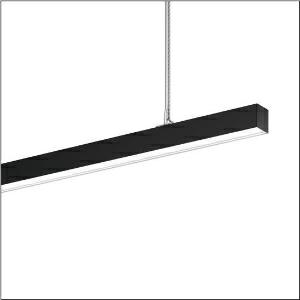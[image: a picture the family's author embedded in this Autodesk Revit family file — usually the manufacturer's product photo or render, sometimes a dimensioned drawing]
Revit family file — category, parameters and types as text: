
# Revit family: silica_r__21_51mx30dc49bb_d1ca
name_source: partatom
category: Lighting Fixtures
units: mm (PartAtom-declared; Revit-internal decimal feet)

## family parameters
Cut with Voids When Loaded = No
Host = Face
Light Source = No
Part Type = Normal
Room Calculation Point = No
Round Connector Dimension = Use Diameter
Shared = No

## types (1)
- --- (1 x LED, 10520 lm, 64.1 W, 4000K)
    Apparent Load = 64 VA
    CIE Flux Codes = 47 79 96 57 100
    Color Rendering = 80
    Color Temperature = 4000K
    Default Elevation = 1800 mm
    Description = Silica® 21, office luminaire, primary optical cover: cover, of PMMA, opal, light emission: direct/indirect distribution, primary light characteristic: symmetric, installation type: suspended mounting, LED, rated luminous flux: 10.520lm, luminous efficacy: 164lm/W, light colour: 840, colour temperature: 4000K, with terminal, 3+2-pole, max. 2.5mm², mains connection: 220..240V, AC, 50/60Hz, rated input power: 64.1W, luminaire housing, of aluminium, jet black (RAL 9005), length: 3.004mm, width: 53mm, height: 53mm, protection rating (complete): IP20, insulation class (complete): insulation class I (protective earthing), certification: CE, permissible operating ambient temperature: 0..+35°C, standard: EN 50419, packaging unit: 1 piece
    Height = 53 mm
    Lamp = 1 x LED
    Lamp Light Flux = 10520 lm
    Lamp Power = 64.1 W
    Lamp count = 1
    Length = 3004 mm
    Luminous efficacy = 164 lm/W
    Manufacturer = Siteco
    ModVariant = No
    Model = 51MX30DC49BB
    Mounting Place = Ceiling
    Mounting Type = Pendant
    Number of Poles = 1
    OnlyDefault = Yes
    Power Factor = 1
    Product Name = Silica® 21
    Product group = office luminaire | ceiling pendant
    ProductGroupID = 902
    Protection Class = Protection class I
    Protection Degree = IP 20
    RLX_Detail_Level = 1
    RLX_Emergency_Light_Flux = 0 lm
    RLX_Emergency_Type = 0
    RLX_Emergency_Type_DB = No
    RlxData = <blob elided: 26041 chars, md5=3b6e2031>
    Socket = socket
    Standby Power = 0 W
    System Light Flux = 10520 lm
    System Power = 64 W
    Type Comments = factory setting: luminous flux: 100 % | dim-lin: 254 | 218 mA
    Type Image = l_1313646.jpg
    URL = http://relux.com
    VarID = @adj_065465
    Voltage = 0 V
    Weight = 0.00 kg
    Width = 53 mm

## geometry (parser evidence)
native form markers: Blend x4, Sweep x14
no freeform markers — native parametric forms only
